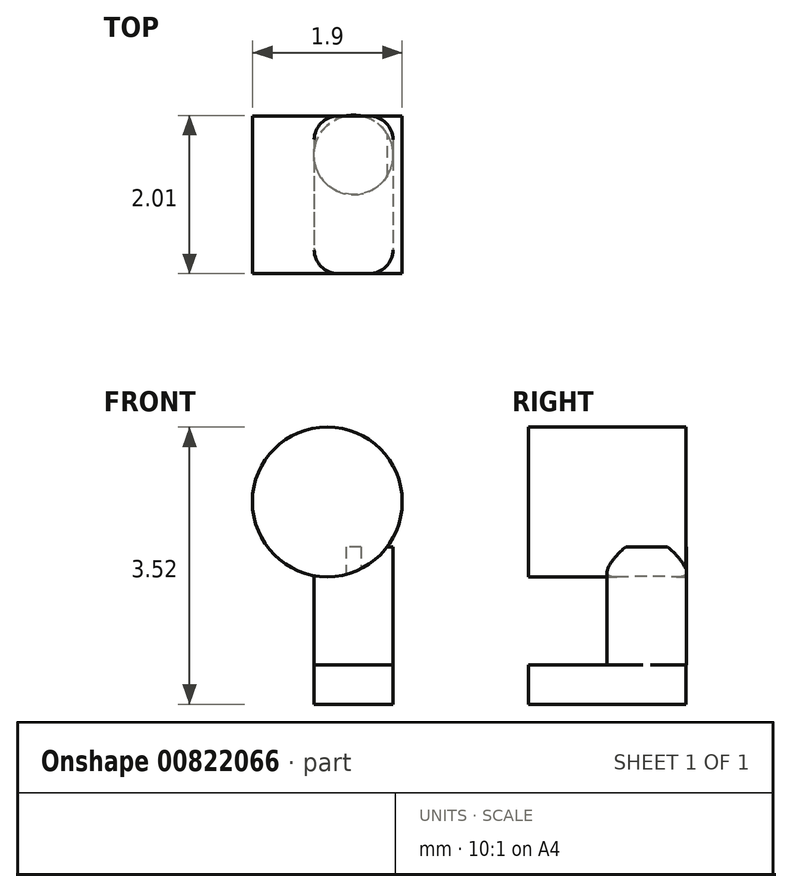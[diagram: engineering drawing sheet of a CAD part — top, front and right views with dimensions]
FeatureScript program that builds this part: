
annotation { "Feature Type Name" : "Feature", "Feature Type Description" : "" }
export const myFeature = defineFeature(function(context is Context, id is Id, definition is map)
    precondition{}
    {
        {
            var Q0;
            Q0=qCreatedBy(makeId("Top.planeOp"),FACE);
            var sketch = newSketch(context, id + "F0", { "sketchPlane" : qUnion([Q0])});
            skLineSegment(sketch, "E0.bottom", {"start": v(-113.84, 13.58) * mm, "end": v(-112.84, 13.58) * mm});
            skLineSegment(sketch, "E0.top", {"start": v(-113.84, 11.58) * mm, "end": v(-112.84, 11.58) * mm});
            skLineSegment(sketch, "E0.left", {"start": v(-113.84, 13.58) * mm, "end": v(-113.84, 11.58) * mm});
            skLineSegment(sketch, "E0.right", {"start": v(-112.84, 13.58) * mm, "end": v(-112.84, 11.58) * mm});
            skSolve(sketch);
        }
        {
            var Q0;
            Q0 = qSketchRegion(id + "F0", true);
            extrude(context, id + "F1", {"entities" : qUnion([Q0]), "depth" : 0.5 * mm, "offsetDistance" : 25 * mm});
        }
        {
            var Q0;
            Q0=makeQuery(id+"F1.opExtrude","SWEPT_EDGE",EDGE,{"disambiguationData":[OSD([sQuery(id+"F0.wireOp",EDGE,"E0.top"),sQuery(id+"F0.wireOp",EDGE,"E0.left")])]});
            var Q1;
            Q1=makeQuery(id+"F1.opExtrude","SWEPT_EDGE",EDGE,{"disambiguationData":[OSD([sQuery(id+"F0.wireOp",EDGE,"E0.bottom"),sQuery(id+"F0.wireOp",EDGE,"E0.right")])]});
            var Q2;
            Q2=makeQuery(id+"F1.opExtrude","SWEPT_EDGE",EDGE,{"disambiguationData":[OSD([sQuery(id+"F0.wireOp",EDGE,"E0.top"),sQuery(id+"F0.wireOp",EDGE,"E0.right")])]});
            var Q3;
            Q3=makeQuery(id+"F1.opExtrude","SWEPT_EDGE",EDGE,{"disambiguationData":[OSD([sQuery(id+"F0.wireOp",EDGE,"E0.bottom"),sQuery(id+"F0.wireOp",EDGE,"E0.left")])]});
            fillet(context, id + "F2", {"entities" : qUnion([Q0, Q1, Q2, Q3]), "radius" : 0.3 * mm, "tangentPropagation" : true, "allowEdgeOverflow" : false});
        }
        {
            var Q0;
            Q0=makeQuery(id+"F1.opExtrude","CAP_FACE",FACE,{"disambiguationData":[OSD([sQuery(id+"F0.wireOp",EDGE,"E0.bottom"),sQuery(id+"F0.wireOp",EDGE,"E0.top"),sQuery(id+"F0.wireOp",EDGE,"E0.left"),sQuery(id+"F0.wireOp",EDGE,"E0.right")])],"isStart":false});
            var sketch = newSketch(context, id + "F3", { "sketchPlane" : qUnion([Q0])});
            skCircle(sketch, "E1", {"center": v(-113.34, 13.09) * mm, "radius": 0.5 * mm});
            skPoint(sketch, "E1.first.point", {"position": v(-113.84, 13) * mm});
            skPoint(sketch, "E1.second.point", {"position": v(-112.84, 13.14) * mm});
            skPoint(sketch, "E1.third.point", {"position": v(-112.84, 13.04) * mm});
            skSolve(sketch);
        }
        {
            var Q0;
            Q0 = qSketchRegion(id + "F3", true);
            extrude(context, id + "F4", {"entities" : qUnion([Q0]), "operationType" : NewBodyOperationType.ADD, "depth" : 1.5 * mm, "offsetDistance" : 25 * mm});
        }
        {
            var Q0;
            Q0=makeQuery(id+"F1.opExtrude","SWEPT_FACE",FACE,{"disambiguationData":[OSD([sQuery(id+"F0.wireOp",EDGE,"E0.bottom")])]});
            var sketch = newSketch(context, id + "F5", { "sketchPlane" : qUnion([Q0])});
            skCircle(sketch, "E2", {"center": v(113.67, 2.57) * mm, "radius": 0.95 * mm});
            skPoint(sketch, "E2.first.point", {"position": v(113.27, 1.7) * mm});
            skPoint(sketch, "E2.second.point", {"position": v(113.88, 3.5) * mm});
            skPoint(sketch, "E2.third.point", {"position": v(114.62, 2.53) * mm});
            skSolve(sketch);
        }
        {
            var Q0;
            Q0 = qSketchRegion(id + "F5", true);
            extrude(context, id + "F6", {"entities" : qUnion([Q0]), "operationType" : NewBodyOperationType.ADD, "oppositeDirection" : true, "depth" : 2 * mm, "offsetDistance" : 25 * mm});
        }
    });
